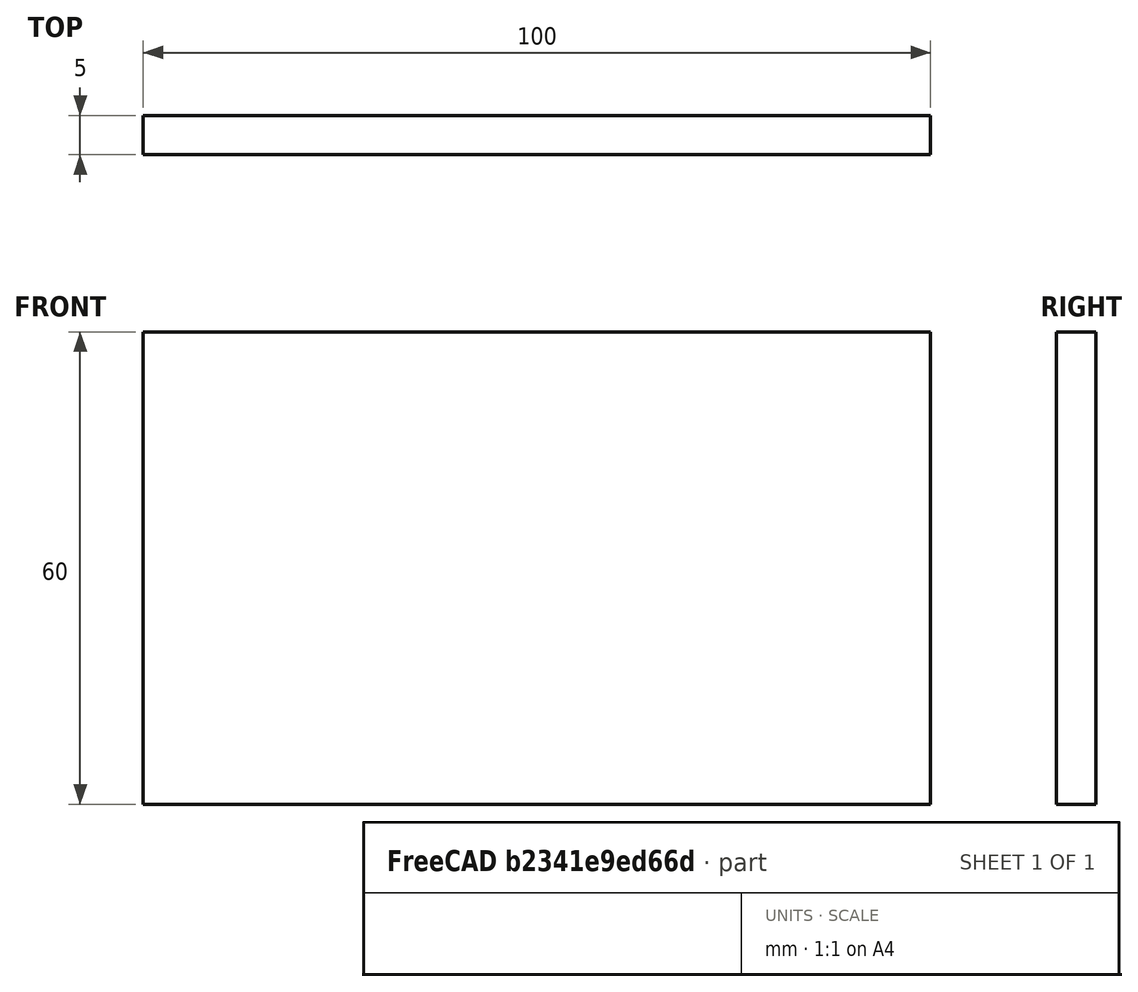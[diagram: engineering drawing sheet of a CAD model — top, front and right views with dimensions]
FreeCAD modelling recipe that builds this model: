
FCSTD DOCUMENT  (FreeCAD 0.16R6712 (Git))
Label: table
License: All rights reserved
LicenseURL: http://en.wikipedia.org/wiki/All_rights_reserved
objects: Sketcher::SketchObject×1, PartDesign::Pad×1, Mesh::Feature×1
note: 3 computed .brp shape members not serialized (recipe doc carries the construction recipe); baked Part::Feature solids carry a one-line shape summary decoded from their .brp

FEATURE [Sketcher::SketchObject] Sketch
  Placement = pos=(0,0,0) rot=(1,0,0;1.5708rad)
  sketch-geometry (4):
    g0: LineSegment StartX=50 StartY=30 StartZ=0 EndX=-50 EndY=30 EndZ=0
    g1: LineSegment StartX=-50 StartY=30 StartZ=0 EndX=-50 EndY=-30 EndZ=0
    g2: LineSegment StartX=-50 StartY=-30 StartZ=0 EndX=50 EndY=-30 EndZ=0
    g3: LineSegment StartX=50 StartY=-30 StartZ=0 EndX=50 EndY=30 EndZ=0
  constraints (11):
    c: Horizontal(g0)
    c: Horizontal(g2)
    c: Vertical(g1)
    c: DistanceX(g-2,g3) = 50
    c: DistanceY(g-1,g2) = -30
    c: Symmetric(g0,g2,g-1)
    c: Symmetric(g1,g3,g-2)
    c: Coincident(g1,g0)
    c: Coincident(g1,g2)
    c: Coincident(g2,g3)
    c: Coincident(g3,g0)
FEATURE [PartDesign::Pad] Pad
  Length = 5
  Length2 = 100
  Placement = pos=(0,0,0) rot=(1,0,0;1.5708rad)
  Sketch = -> Sketch
  Type = 0
FEATURE [Mesh::Feature] Mesh  label="Pad (Meshed)"
